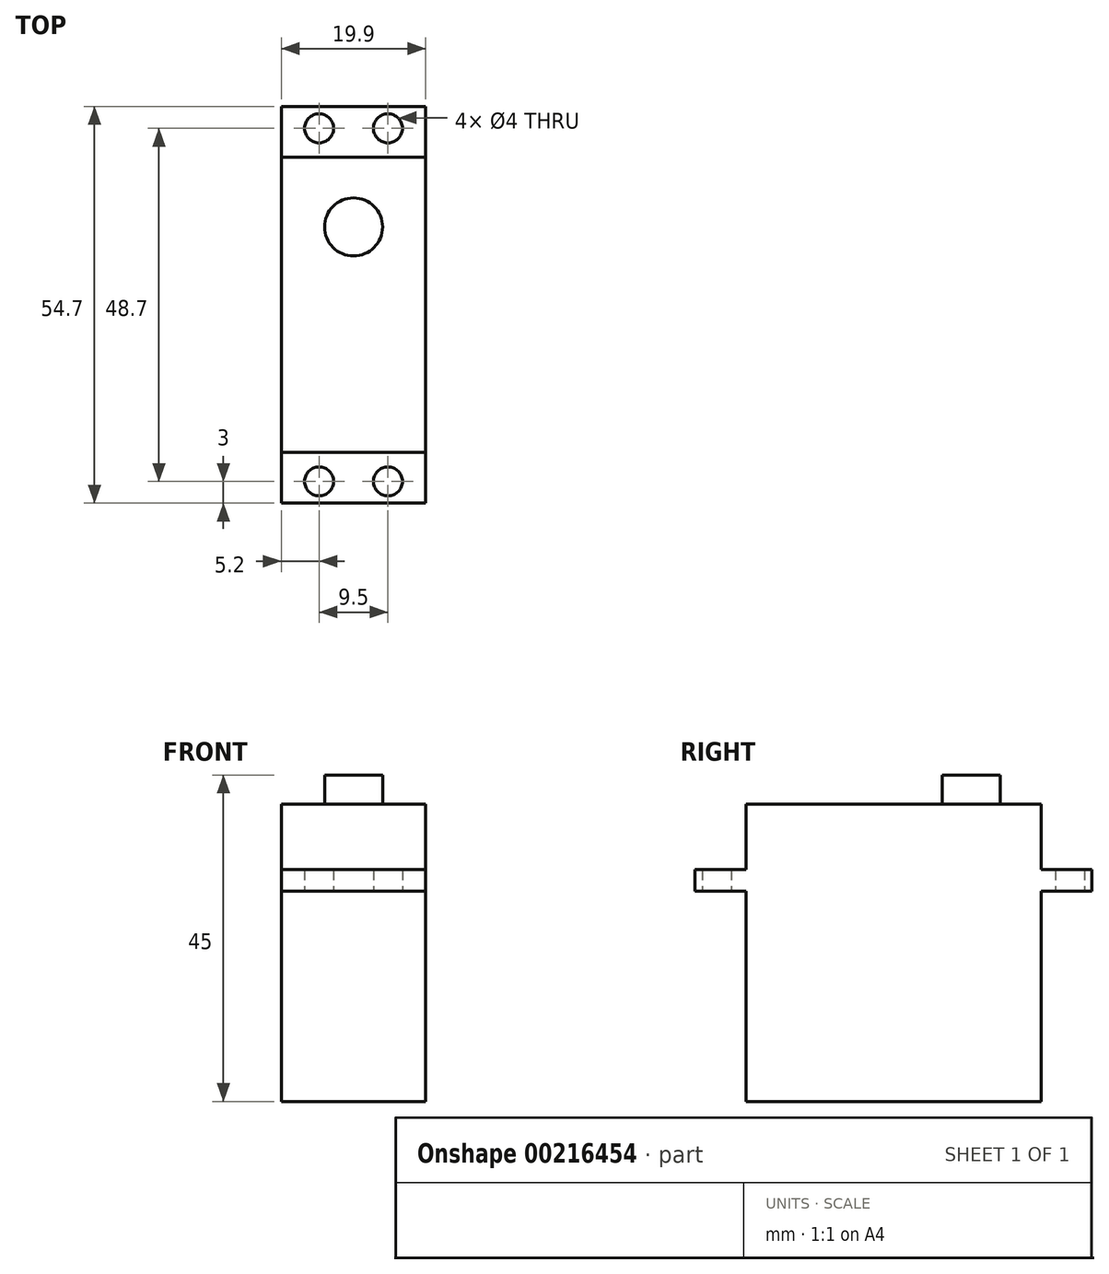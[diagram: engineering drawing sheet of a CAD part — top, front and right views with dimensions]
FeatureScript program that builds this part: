
annotation { "Feature Type Name" : "Feature", "Feature Type Description" : "" }
export const myFeature = defineFeature(function(context is Context, id is Id, definition is map)
    precondition{}
    {
        {
            var Q0;
            Q0=qCreatedBy(makeId("Top.planeOp"),FACE);
            var sketch = newSketch(context, id + "F0", { "sketchPlane" : qUnion([Q0])});
            skLineSegment(sketch, "E0.bottom", {"start": v(-9.95, 9.6) * mm, "end": v(9.95, 9.6) * mm});
            skLineSegment(sketch, "E0.top", {"start": v(-9.95, -31.1) * mm, "end": v(9.95, -31.1) * mm});
            skLineSegment(sketch, "E0.left", {"start": v(-9.95, 9.6) * mm, "end": v(-9.95, -31.1) * mm});
            skLineSegment(sketch, "E0.right", {"start": v(9.95, 9.6) * mm, "end": v(9.95, -31.1) * mm});
            skPoint(sketch, "E1", {"position": v(0, 9.6) * mm});
            skSolve(sketch);
        }
        {
            var Q0;
            Q0 = qSketchRegion(id + "F0", true);
            extrude(context, id + "F1", {"entities" : qUnion([Q0]), "depth" : 41 * mm});
        }
        {
            var Q0;
            Q0=qCreatedBy(makeId("Top.planeOp"),FACE);
            cPlane(context, id + "F2", {"entities" : qUnion([Q0]), "cplaneType" : CPlaneType.OFFSET, "offset" : 29 * mm, "width" : 150 * mm, "height" : 150 * mm});
        }
        {
            var Q0;
            Q0=qCreatedBy(id+"F2.planeOp",FACE);
            var sketch = newSketch(context, id + "F3", { "sketchPlane" : qUnion([Q0])});
            skLineSegment(sketch, "E2", {"start": v(-9.95, 9.6) * mm, "end": v(9.95, 9.6) * mm});
            skLineSegment(sketch, "E3", {"start": v(9.95, 9.6) * mm, "end": v(9.95, 16.6) * mm});
            skLineSegment(sketch, "E4", {"start": v(9.95, 16.6) * mm, "end": v(-9.95, 16.6) * mm});
            skLineSegment(sketch, "E5", {"start": v(-9.95, 16.6) * mm, "end": v(-9.95, 9.6) * mm});
            skCircle(sketch, "E6", {"center": v(4.75, 13.6) * mm, "radius": 2 * mm});
            skCircle(sketch, "E7.MirrorC", {"center": v(-4.75, 13.6) * mm, "radius": 2 * mm});
            skLineSegment(sketch, "E8", {"start": v(-9.95, -10.75) * mm, "end": v(9.95, -10.75) * mm, "construction": true});
            skLineSegment(sketch, "E9.MirrorCS", {"start": v(-9.95, -31.1) * mm, "end": v(9.95, -31.1) * mm});
            skLineSegment(sketch, "E10.MirrorCS", {"start": v(9.95, -31.1) * mm, "end": v(9.95, -38.1) * mm});
            skLineSegment(sketch, "E11.MirrorCS", {"start": v(9.95, -38.1) * mm, "end": v(-9.95, -38.1) * mm});
            skLineSegment(sketch, "E12.MirrorCS", {"start": v(-9.95, -38.1) * mm, "end": v(-9.95, -31.1) * mm});
            skCircle(sketch, "E13.MirrorC", {"center": v(4.75, -35.1) * mm, "radius": 2 * mm});
            skCircle(sketch, "E14.MirrorC", {"center": v(-4.75, -35.1) * mm, "radius": 2 * mm});
            skSolve(sketch);
        }
        {
            var Q0;
            Q0 = qSketchRegion(id + "F3", true);
            extrude(context, id + "F4", {"entities" : qUnion([Q0]), "operationType" : NewBodyOperationType.ADD, "depth" : 3 * mm});
        }
        {
            var Q0;
            Q0=makeQuery(id+"F1.opExtrude","CAP_FACE",FACE,{"disambiguationData":[OSD([sQuery(id+"F0.wireOp",EDGE,"E0.bottom"),sQuery(id+"F0.wireOp",EDGE,"E0.top"),sQuery(id+"F0.wireOp",EDGE,"E0.left"),sQuery(id+"F0.wireOp",EDGE,"E0.right")])],"isStart":false});
            var sketch = newSketch(context, id + "F5", { "sketchPlane" : qUnion([Q0])});
            skCircle(sketch, "E15", {"center": v(0, 0) * mm, "radius": 4 * mm});
            skSolve(sketch);
        }
        {
            var Q0;
            Q0 = qSketchRegion(id + "F5", true);
            extrude(context, id + "F6", {"entities" : qUnion([Q0]), "operationType" : NewBodyOperationType.ADD, "depth" : 4 * mm});
        }
    });
